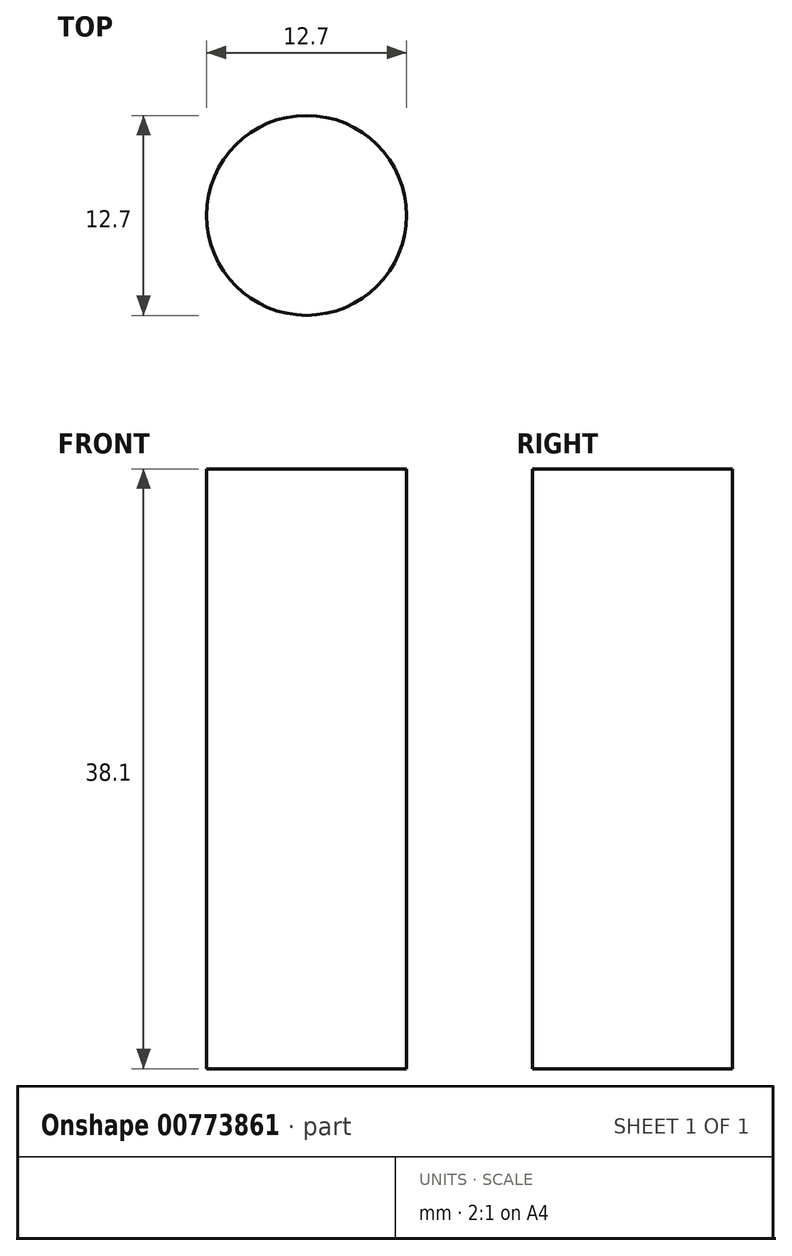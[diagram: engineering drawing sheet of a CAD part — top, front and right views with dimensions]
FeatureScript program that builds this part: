
annotation { "Feature Type Name" : "Feature", "Feature Type Description" : "" }
export const myFeature = defineFeature(function(context is Context, id is Id, definition is map)
    precondition{}
    {
        {
            var Q0;
            Q0=qCreatedBy(makeId("Top.planeOp"),FACE);
            var sketch = newSketch(context, id + "F0", { "sketchPlane" : qUnion([Q0])});
            skCircle(sketch, "E0", {"center": v(0, 0) * mm, "radius": 6.35 * mm});
            skSolve(sketch);
        }
        {
            var Q0;
            Q0 = qSketchRegion(id + "F0", true);
            extrude(context, id + "F1", {"entities" : qUnion([Q0]), "flatOperationType" : FlatOperationType.REMOVE, "depth" : 38.1 * mm, "offsetDistance" : 25.4 * mm, "domain" : OperationDomain.MODEL});
        }
    });
